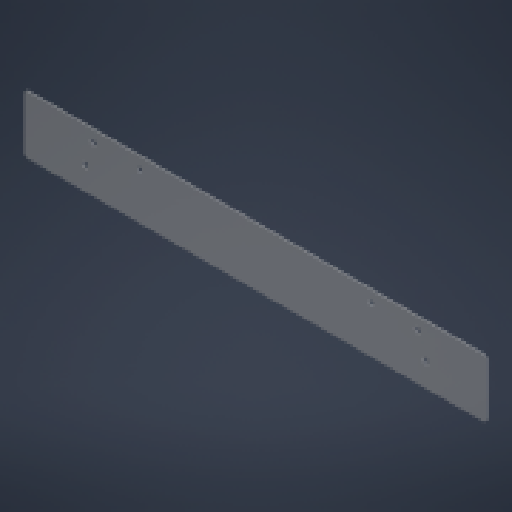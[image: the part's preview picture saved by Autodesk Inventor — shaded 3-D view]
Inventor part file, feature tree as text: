
AUTODESK INVENTOR PART (.ipt)
format: ipt  version: 2024 (Build 280153000, 153)  size: 236,544 bytes
history: native  units: in
note: dims shown in document units (in); Inventor stores cm internally (conversion verified against a paired STEP export)
features: sketch x2, extrude x1, hole x1
ambient origin geometry x8: Origin, YZ Plane, XZ Plane, XY Plane, X Axis, Y Axis, Z Axis, Center Point
bodies: Solid1 (feature_tree)
feature tree (4):
  extrude  "Extrusion1"  Depth=0.0625in TaperAngle=0.0deg
  hole  "Hole1"  [1 undecoded]
  sketch  "Sketch1"  dims[d1=2.0in d2=0.0625in d3=0.0in]
  sketch  "Sketch2"  dims[d4=2.25in d5=2.0in d7=0.25in d11=2.0in d12=0.1875in d13=0.75in d14=0.375in d15=0.25in d16=0.5635in d17=1.0in d18=0.8108in d19=0.125in d20=0.125in d21=0.5in d22=0.5in d23=0.5in d24=0.375in d25=0.375in d26=0.125in]
note: 1 required parameter value undecoded (feature->parameter linkage not recoverable at this tier; creation-order binding heuristic only, values carry confidence <= 0.55)
